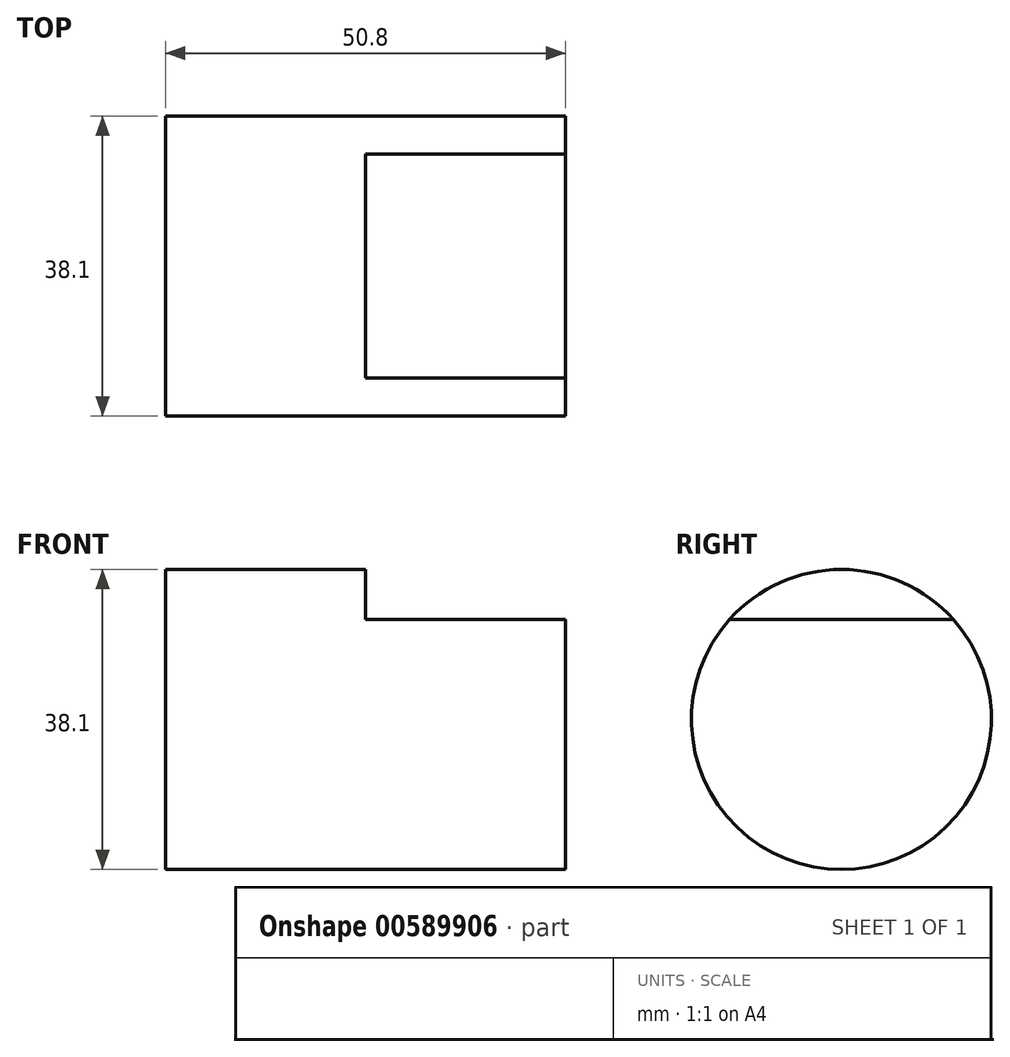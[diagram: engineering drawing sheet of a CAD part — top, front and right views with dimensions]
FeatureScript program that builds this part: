
annotation { "Feature Type Name" : "Feature", "Feature Type Description" : "" }
export const myFeature = defineFeature(function(context is Context, id is Id, definition is map)
    precondition{}
    {
        {
            var Q0;
            Q0=qCreatedBy(makeId("Right.planeOp"),FACE);
            var sketch = newSketch(context, id + "F0", { "sketchPlane" : qUnion([Q0])});
            skCircle(sketch, "E0", {"center": v(0, 0) * mm, "radius": 19.05 * mm});
            skSolve(sketch);
        }
        {
            var Q0;
            Q0=makeQuery(id+"F0.imprint","IMPRINT",FACE,{"disambiguationData":[TD([[makeQuery(id+"F0.imprint","IMPRINT",EDGE,{"derivedFrom":sQuery(id+"F0.wireOp",EDGE,"E0")}),1.0]])]});
            extrude(context, id + "F1", {"entities" : qUnion([Q0]), "depth" : 50.8 * mm, "offsetDistance" : 25.4 * mm});
        }
        {
            var Q0;
            Q0=makeQuery(id+"F1.opExtrude","CAP_FACE",FACE,{"disambiguationData":[OSD([sQuery(id+"F0.wireOp",EDGE,"E0")])],"isStart":false});
            cPlane(context, id + "F2", {"entities" : qUnion([Q0]), "cplaneType" : CPlaneType.OFFSET, "offset" : 25.4 * mm, "oppositeDirection" : true, "width" : 152.4 * mm, "height" : 152.4 * mm});
        }
        {
            var Q0;
            Q0=qCreatedBy(id+"F2.planeOp",FACE);
            var sketch = newSketch(context, id + "F3", { "sketchPlane" : qUnion([Q0])});
            skLineSegment(sketch, "E1", {"start": v(-14.2, 12.7) * mm, "end": v(14.2, 12.7) * mm});
            skArc(sketch, "E2", {"start": v(14.2, 12.7) * mm, "mid": v(0, 19.05) * mm, "end": v(-14.2, 12.7) * mm});
            skSolve(sketch);
        }
        {
            var Q0;
            Q0 = qSketchRegion(id + "F3", true);
            extrude(context, id + "F4", {"entities" : qUnion([Q0]), "operationType" : NewBodyOperationType.REMOVE, "depth" : 25.4 * mm, "offsetDistance" : 25.4 * mm});
        }
    });
